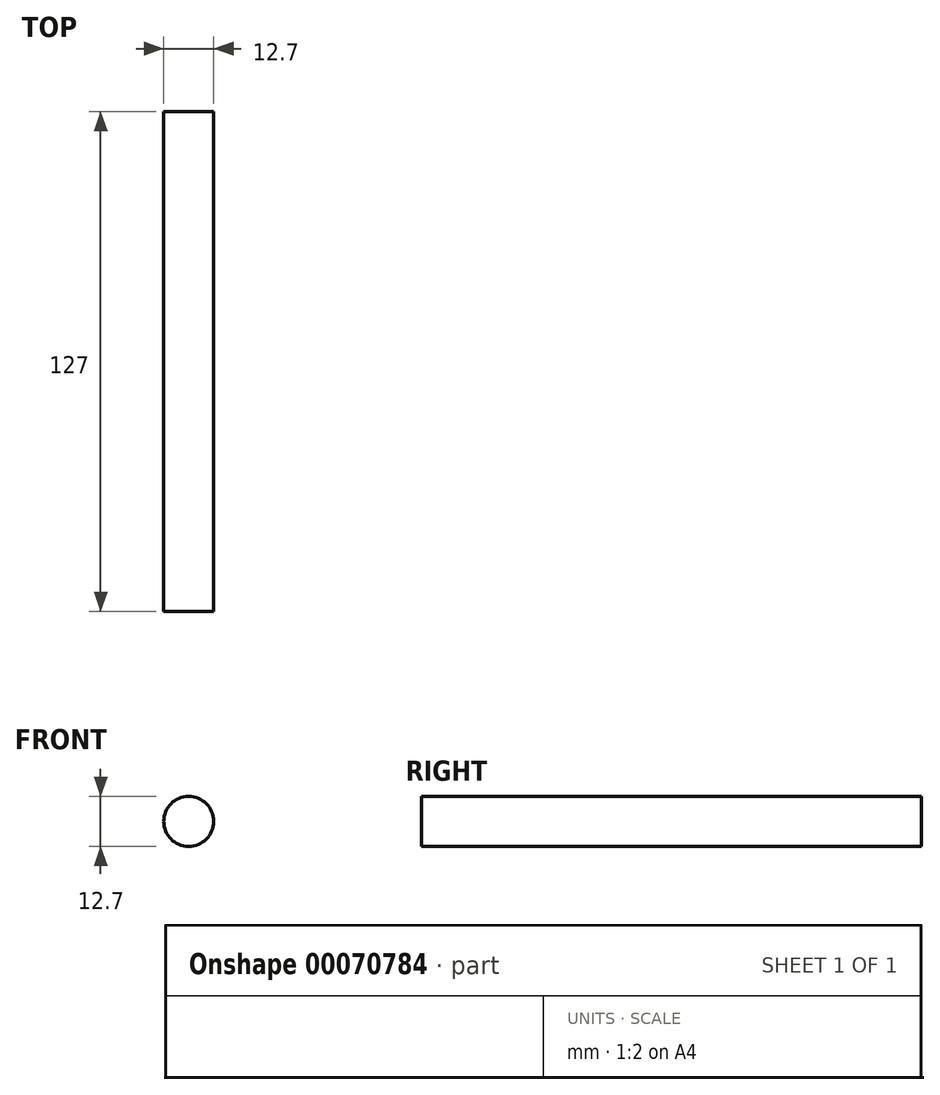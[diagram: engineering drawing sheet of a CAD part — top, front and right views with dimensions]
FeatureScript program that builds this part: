
annotation { "Feature Type Name" : "Feature", "Feature Type Description" : "" }
export const myFeature = defineFeature(function(context is Context, id is Id, definition is map)
    precondition{}
    {
        {
            var Q0;
            Q0=qCreatedBy(makeId("Front.planeOp"),FACE);
            var sketch = newSketch(context, id + "F0", { "sketchPlane" : qUnion([Q0])});
            skCircle(sketch, "E0", {"center": v(0, 0) * mm, "radius": 6.35 * mm});
            skSolve(sketch);
        }
        {
            var Q0;
            Q0 = qSketchRegion(id + "F0", true);
            extrude(context, id + "F1", {"entities" : qUnion([Q0]), "depth" : 127 * mm});
        }
    });
